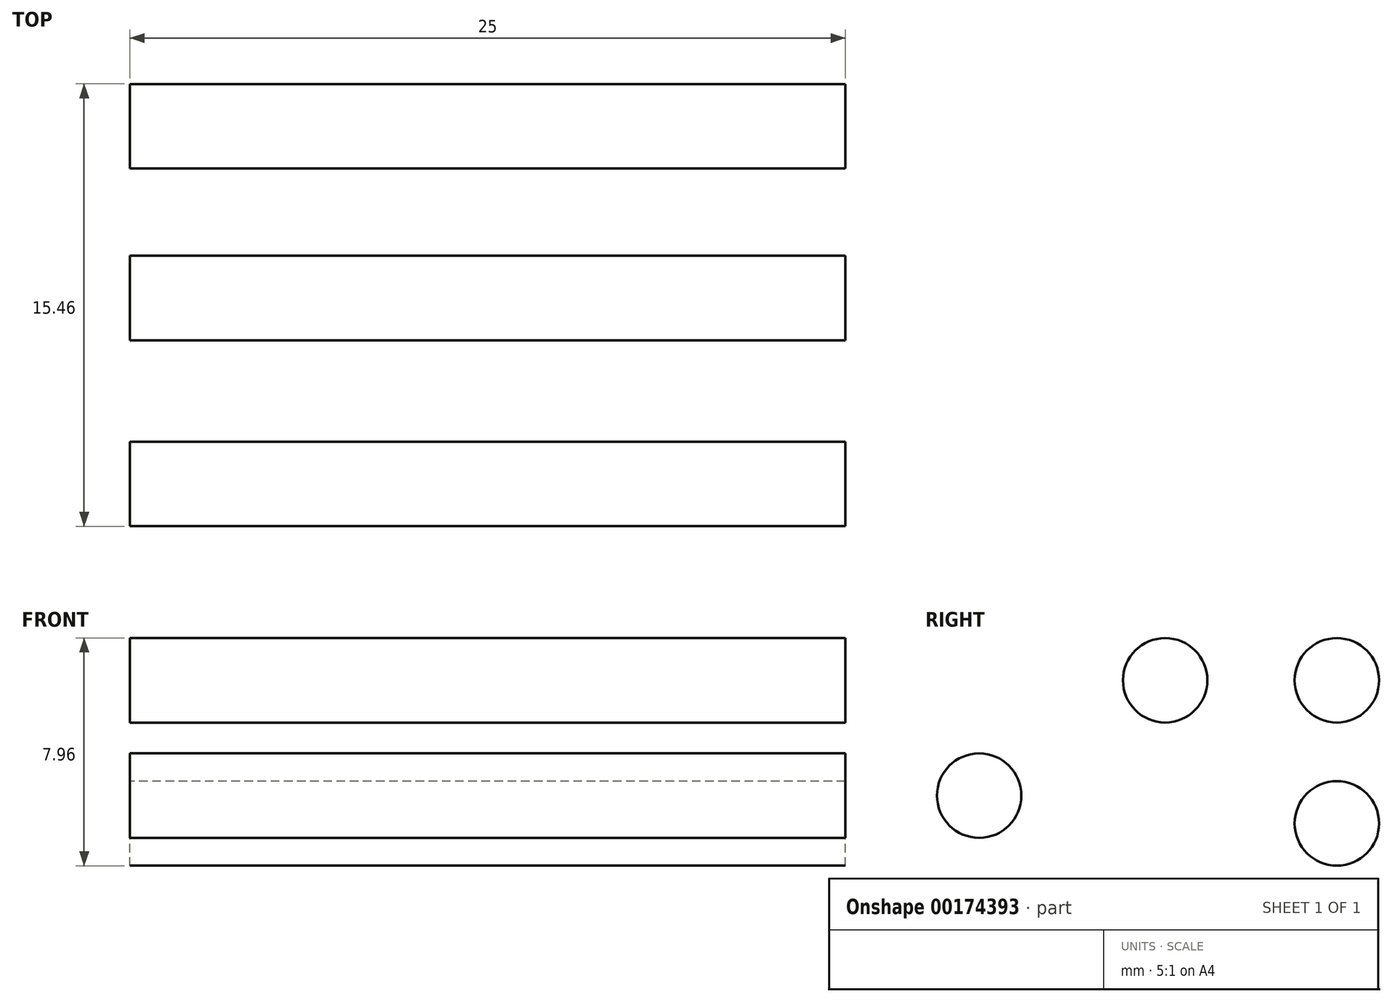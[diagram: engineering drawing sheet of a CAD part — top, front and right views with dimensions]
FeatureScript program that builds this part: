
annotation { "Feature Type Name" : "Feature", "Feature Type Description" : "" }
export const myFeature = defineFeature(function(context is Context, id is Id, definition is map)
    precondition{}
    {
        {
            var Q0;
            Q0=qCreatedBy(makeId("Right.planeOp"),FACE);
            var sketch = newSketch(context, id + "F0", { "sketchPlane" : qUnion([Q0])});
            skCircle(sketch, "E0", {"center": v(0, 0) * mm, "radius": 1.48 * mm});
            skCircle(sketch, "E1", {"center": v(0, 5) * mm, "radius": 1.48 * mm});
            skCircle(sketch, "E2", {"center": v(-6, 5) * mm, "radius": 1.48 * mm});
            skCircle(sketch, "E3", {"center": v(-12.5, 0.97) * mm, "radius": 1.48 * mm});
            skSolve(sketch);
        }
        {
            var Q0;
            Q0=makeQuery(id+"F0.imprint","IMPRINT",FACE,{"disambiguationData":[TD([[makeQuery(id+"F0.imprint","IMPRINT",EDGE,{"derivedFrom":sQuery(id+"F0.wireOp",EDGE,"E3")}),1.0]])]});
            var Q1;
            Q1=makeQuery(id+"F0.imprint","IMPRINT",FACE,{"disambiguationData":[TD([[makeQuery(id+"F0.imprint","IMPRINT",EDGE,{"derivedFrom":sQuery(id+"F0.wireOp",EDGE,"E2")}),1.0]])]});
            var Q2;
            Q2=makeQuery(id+"F0.imprint","IMPRINT",FACE,{"disambiguationData":[TD([[makeQuery(id+"F0.imprint","IMPRINT",EDGE,{"derivedFrom":sQuery(id+"F0.wireOp",EDGE,"E1")}),1.0]])]});
            var Q3;
            Q3=makeQuery(id+"F0.imprint","IMPRINT",FACE,{"disambiguationData":[TD([[makeQuery(id+"F0.imprint","IMPRINT",EDGE,{"derivedFrom":sQuery(id+"F0.wireOp",EDGE,"E0")}),1.0]])]});
            extrude(context, id + "F1", {"entities" : qUnion([Q0, Q1, Q2, Q3]), "depth" : 25 * mm});
        }
    });
